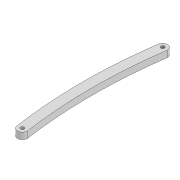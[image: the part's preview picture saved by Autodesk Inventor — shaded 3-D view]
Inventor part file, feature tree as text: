
AUTODESK INVENTOR PART (.ipt)
format: ipt  version: 2022 (Build 260153000, 153)  size: 91,136 bytes
history: native  units: mm
features: extrude x1, sketch x1
ambient origin geometry x8: Origin, YZ Plane, XZ Plane, XY Plane, X Axis, Y Axis, Z Axis, Center Point
bodies: Solid1 (feature_tree)
feature tree (2):
  extrude  "Extrusion1"  Depth=300.0mm
  sketch  "Sketch1"  dims[d0=2.2mm d1=2.2mm d2=6.0mm d3=85.9mm d6=4.0mm d7=0.0mm d10=300.0mm d11=300.0mm]
